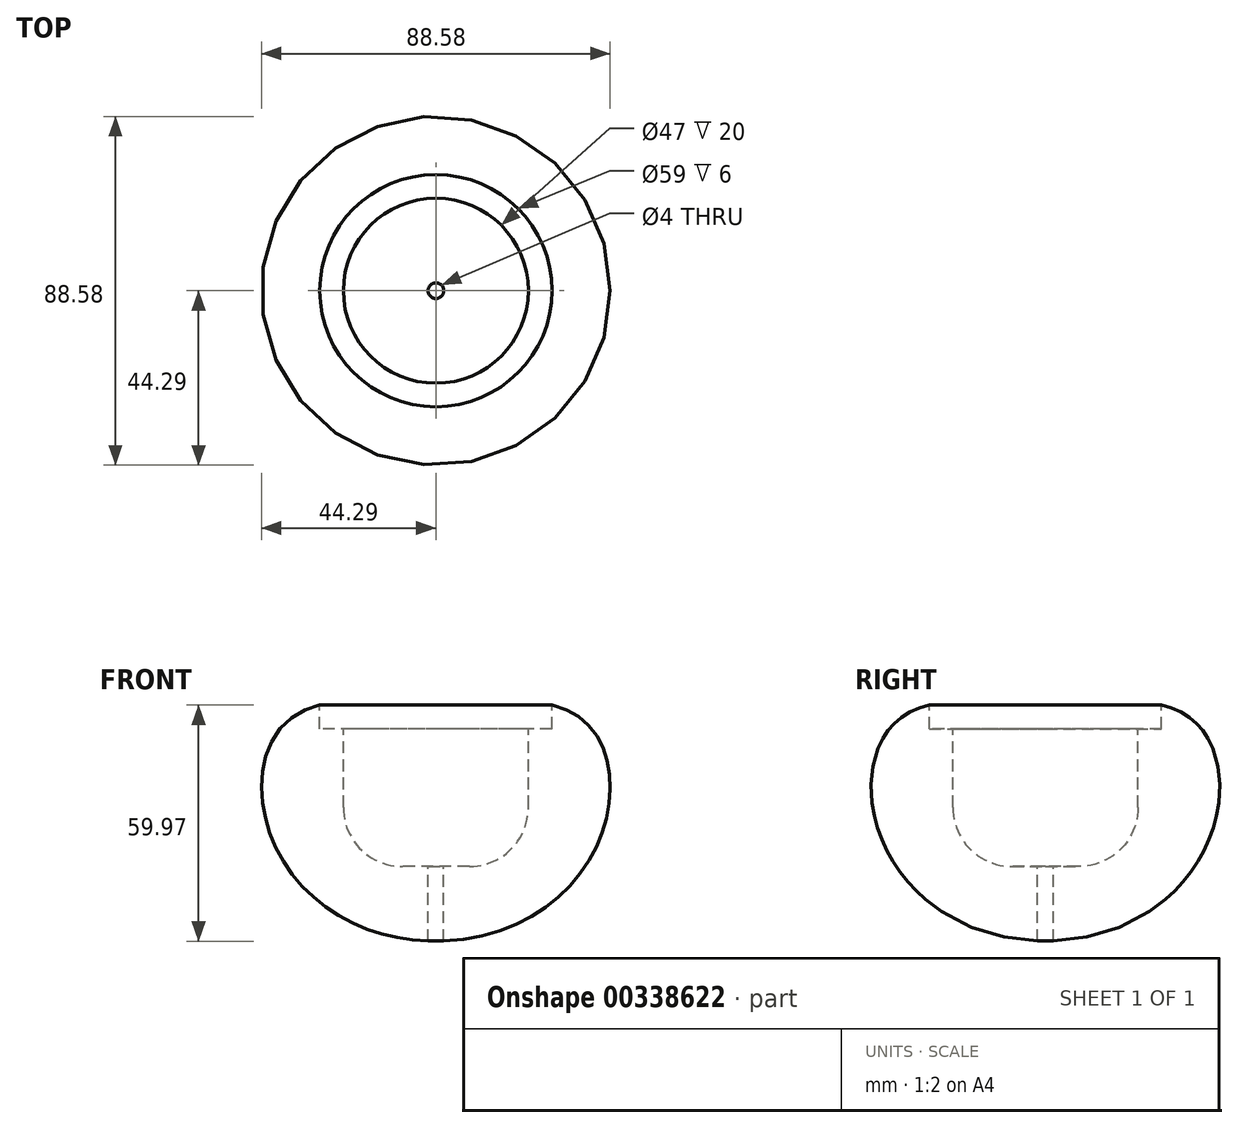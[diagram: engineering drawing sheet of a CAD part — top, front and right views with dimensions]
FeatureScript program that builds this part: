
annotation { "Feature Type Name" : "Feature", "Feature Type Description" : "" }
export const myFeature = defineFeature(function(context is Context, id is Id, definition is map)
    precondition{}
    {
        {
            var Q0;
            Q0=qCreatedBy(makeId("Front.planeOp"),FACE);
            var sketch = newSketch(context, id + "F0", { "sketchPlane" : qUnion([Q0])});
            skLineSegment(sketch, "E0", {"start": v(23.5, 29.69) * mm, "end": v(29.5, 29.69) * mm});
            skLineSegment(sketch, "E1", {"start": v(29.5, 29.69) * mm, "end": v(29.5, 35.69) * mm});
            skLineSegment(sketch, "E2", {"start": v(23.5, 29.69) * mm, "end": v(23.5, 9.69) * mm});
            skLineSegment(sketch, "E3", {"start": v(23.5, 9.69) * mm, "end": v(23.5, 9.69) * mm});
            skLineSegment(sketch, "E4", {"start": v(8.5, -5.31) * mm, "end": v(0, -5.31) * mm});
            skPoint(sketch, "E5.visualSharp", {"position": v(23.5, -5.31) * mm});
            skArc(sketch, "E5.filletArc", {"start": v(8.5, -5.31) * mm, "mid": v(19.1, -0.92) * mm, "end": v(23.5, 9.69) * mm});
            skLineSegment(sketch, "E6", {"start": v(43, 38.22) * mm, "end": v(43, -53.52) * mm, "construction": true});
            skLineSegment(sketch, "E7", {"start": v(0, 64.06) * mm, "end": v(0, -46.95) * mm, "construction": true});
            skLineSegment(sketch, "E8", {"start": v(29.5, 35.69) * mm, "end": v(152.51, 35.69) * mm, "construction": true});
            skLineSegment(sketch, "E9", {"start": v(0, -24.31) * mm, "end": v(151.95, -24.31) * mm, "construction": true});
            skPoint(sketch, "E10", {"position": v(43, 35.69) * mm});
            skPoint(sketch, "E11", {"position": v(43, -24.31) * mm});
            skPoint(sketch, "E12", {"position": v(43, 5.69) * mm});
            skFitSpline(sketch, "E13", {"points": [v(29.5, 35.69) * mm, v(43, 5.69) * mm, v(0, -24.31) * mm], "startDerivative": vector(91.63, -20.36) * mm, "endDerivative": vector(-121.99, 0) * mm});
            skPoint(sketch, "E14", {"position": v(29.5, 32.69) * mm});
            skLineSegment(sketch, "E15", {"start": v(0, -5.31) * mm, "end": v(0, -24.31) * mm});
            skSolve(sketch);
        }
        {
            var Q0;
            Q0=makeQuery(id+"F0.imprint","IMPRINT",FACE,{"disambiguationData":[TD([[makeQuery(id+"F0.imprint","IMPRINT",EDGE,{"derivedFrom":sQuery(id+"F0.wireOp",EDGE,"E0")}),-1.0]])]});
            var Q1;
            Q1=sQuery(id+"F0.wireOp",EDGE,"E7");
            revolve(context, id + "F1", {"entities" : qUnion([Q0]), "axis" : qUnion([Q1]), "revolveType" : RevolveType.FULL});
        }
        {
            var Q0;
            Q0=qCreatedBy(makeId("Top.planeOp"),FACE);
            var sketch = newSketch(context, id + "F2", { "sketchPlane" : qUnion([Q0])});
            skCircle(sketch, "E16", {"center": v(0, 0) * mm, "radius": 2 * mm});
            skSolve(sketch);
        }
        {
            var Q0;
            Q0=makeQuery(id+"F2.imprint","IMPRINT",FACE,{"disambiguationData":[TD([[makeQuery(id+"F2.imprint","IMPRINT",EDGE,{"derivedFrom":sQuery(id+"F2.wireOp",EDGE,"E16")}),1.0]])]});
            var Q1;
            Q1=sQuery(id+"F2.wireOp",EDGE,"E16");
            extrude(context, id + "F3", {"entities" : qUnion([Q0]), "operationType" : NewBodyOperationType.REMOVE, "surfaceEntities" : qUnion([Q1]), "endBound" : BoundingType.THROUGH_ALL, "oppositeDirection" : true, "depth" : 60 * mm});
        }
    });
